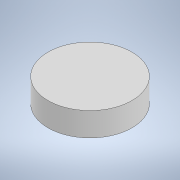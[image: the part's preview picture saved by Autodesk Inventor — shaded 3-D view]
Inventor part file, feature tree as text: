
AUTODESK INVENTOR PART (.ipt)
format: ipt  version: 2020 (Build 240168000, 168)  size: 88,576 bytes
history: native  units: in
note: dims shown in document units (in); Inventor stores cm internally (conversion verified against a paired STEP export)
features: extrude x1, sketch x1
ambient origin geometry x8: Origin, YZ Plane, XZ Plane, XY Plane, X Axis, Y Axis, Z Axis, Center Point
bodies: Solid1 (feature_tree)
feature tree (2):
  extrude  "Extrusion1"  Depth=0.2362in TaperAngle=0.0deg
  sketch  "Sketch1"  dims[d0=0.8366in d1=0.2362in d2=0.0in]
